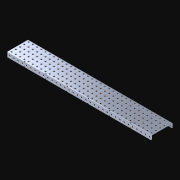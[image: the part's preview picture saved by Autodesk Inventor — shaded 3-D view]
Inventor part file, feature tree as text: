
AUTODESK INVENTOR PART (.ipt)
format: ipt  version: 2021 (Build 250183000, 183)  size: 2,489,344 bytes
history: native  units: in
note: dims shown in document units (in); Inventor stores cm internally (conversion verified against a paired STEP export)
features: extrude x239, other x239, sketch x4, pattern_linear x3
ambient origin geometry x8: Origin, YZ Plane, XZ Plane, XY Plane, X Axis, Y Axis, Z Axis, Center Point
bodies: Solid1 (feature_tree)
feature tree (485):
  pattern_linear  "Rectangular Pattern1"  Spacing1=0.182in  [1 undecoded]
  pattern_linear  "Rectangular Pattern2"  Spacing1=0.046in  [1 undecoded]
  pattern_linear  "Rectangular Pattern3"  Spacing1=0.5in  [1 undecoded]
  extrude  "Extrusion1"  Depth=0.046in
  sketch  "Sketch1"  dims[d0=0.182in]
  other  "Srf1"
  sketch  "Sketch2"  dims[d1=0.046in d2=0.0in]
  other  "Srf2"
  sketch  "Sketch3"  dims[d3=0.182in]
  other  "Srf3"
  other  "Srf4"
  other  "Srf5"
  other  "Srf6"
  other  "Srf7"
  other  "Srf8"
  other  "Srf9"
  other  "Srf10"
  other  "Srf11"
  other  "Srf12"
  other  "Srf13"
  other  "Srf14"
  other  "Srf15"
  other  "Srf16"
  other  "Srf17"
  other  "Srf18"
  other  "Srf19"
  other  "Srf20"
  other  "Srf21"
  other  "Srf22"
  other  "Srf23"
  other  "Srf24"
  other  "Srf25"
  other  "Srf26"
  other  "Srf27"
  other  "Srf28"
  other  "Srf29"
  other  "Srf30"
  other  "Srf31"
  other  "Srf32"
  other  "Srf33"
  other  "Srf34"
  other  "Srf35"
  other  "Srf36"
  other  "Srf38"
  other  "Srf39"
  other  "Srf40"
  other  "Srf41"
  other  "Srf42"
  other  "Srf43"
  other  "Srf44"
  other  "Srf45"
  other  "Srf46"
  other  "Srf47"
  other  "Srf48"
  other  "Srf49"
  other  "Srf50"
  other  "Srf51"
  other  "Srf52"
  other  "Srf53"
  other  "Srf54"
  other  "Srf55"
  other  "Srf56"
  other  "Srf57"
  other  "Srf58"
  other  "Srf59"
  other  "Srf60"
  other  "Srf61"
  other  "Srf62"
  other  "Srf63"
  other  "Srf64"
  other  "Srf65"
  other  "Srf66"
  other  "Srf67"
  other  "Srf68"
  other  "Srf69"
  other  "Srf70"
  other  "Srf72"
  other  "Srf73"
  other  "Srf74"
  other  "Srf75"
  other  "Srf76"
  other  "Srf77"
  other  "Srf78"
  other  "Srf79"
  other  "Srf80"
  other  "Srf81"
  other  "Srf82"
  other  "Srf83"
  other  "Srf84"
  other  "Srf85"
  other  "Srf86"
  other  "Srf87"
  other  "Srf88"
  other  "Srf89"
  other  "Srf90"
  other  "Srf91"
  other  "Srf92"
  other  "Srf93"
  other  "Srf94"
  other  "Srf95"
  other  "Srf96"
  other  "Srf97"
  other  "Srf98"
  other  "Srf99"
  other  "Srf100"
  other  "Srf101"
  other  "Srf102"
  other  "Srf103"
  other  "Srf104"
  other  "Srf105"
  other  "Srf107"
  other  "Srf108"
  other  "Srf109"
  other  "Srf110"
  other  "Srf111"
  other  "Srf112"
  other  "Srf113"
  other  "Srf114"
  other  "Srf115"
  other  "Srf116"
  other  "Srf117"
  other  "Srf118"
  other  "Srf119"
  other  "Srf120"
  other  "Srf121"
  other  "Srf122"
  other  "Srf123"
  other  "Srf124"
  other  "Srf125"
  other  "Srf126"
  other  "Srf127"
  other  "Srf128"
  other  "Srf129"
  other  "Srf130"
  other  "Srf131"
  other  "Srf132"
  other  "Srf133"
  other  "Srf134"
  other  "Srf135"
  other  "Srf136"
  other  "Srf137"
  other  "Srf138"
  other  "Srf139"
  other  "Srf140"
  other  "Srf142"
  other  "Srf143"
  other  "Srf144"
  other  "Srf145"
  other  "Srf146"
  other  "Srf147"
  other  "Srf148"
  other  "Srf149"
  other  "Srf150"
  other  "Srf151"
  other  "Srf152"
  other  "Srf153"
  other  "Srf154"
  other  "Srf155"
  other  "Srf156"
  other  "Srf157"
  other  "Srf158"
  other  "Srf159"
  other  "Srf160"
  other  "Srf161"
  other  "Srf162"
  other  "Srf163"
  other  "Srf164"
  other  "Srf165"
  other  "Srf166"
  other  "Srf167"
  other  "Srf168"
  other  "Srf169"
  other  "Srf170"
  other  "Srf171"
  other  "Srf172"
  other  "Srf173"
  other  "Srf174"
  other  "Srf175"
  other  "Srf177"
  other  "Srf178"
  other  "Srf179"
  other  "Srf180"
  other  "Srf181"
  other  "Srf182"
  other  "Srf183"
  other  "Srf184"
  other  "Srf185"
  other  "Srf186"
  other  "Srf187"
  other  "Srf188"
  other  "Srf189"
  other  "Srf190"
  other  "Srf191"
  other  "Srf192"
  other  "Srf193"
  other  "Srf194"
  other  "Srf195"
  other  "Srf196"
  other  "Srf197"
  other  "Srf198"
  other  "Srf199"
  other  "Srf200"
  other  "Srf201"
  other  "Srf202"
  other  "Srf203"
  other  "Srf204"
  other  "Srf205"
  other  "Srf206"
  other  "Srf207"
  other  "Srf208"
  other  "Srf209"
  other  "Srf210"
  other  "Srf212"
  other  "Srf213"
  other  "Srf214"
  other  "Srf215"
  other  "Srf216"
  other  "Srf217"
  other  "Srf218"
  other  "Srf219"
  other  "Srf220"
  other  "Srf221"
  other  "Srf222"
  other  "Srf223"
  other  "Srf224"
  other  "Srf225"
  other  "Srf226"
  other  "Srf227"
  other  "Srf228"
  other  "Srf229"
  other  "Srf230"
  other  "Srf231"
  other  "Srf232"
  other  "Srf233"
  other  "Srf234"
  other  "Srf235"
  other  "Srf236"
  other  "Srf237"
  other  "Srf238"
  other  "Srf239"
  other  "Srf240"
  other  "Srf241"
  other  "Srf242"
  other  "Srf243"
  other  "Srf244"
  sketch  "Sketch4"  dims[d4=0.046in d5=0.0in d6=0.182in d7=0.046in d8=0.0in d11=0.5in d12=13.3858in d14=0.5in d15=1.9685in d17=0.5in d18=13.3858in d20=0.5in d21=0.5in d22=0.0in]
  parser-record x1  (decoder bookkeeping rows leaked as tree rows — omitted from the tree; the rows remain in map.json)
  extrude  "ExtrusionSrf1"  Depth=0.046in
  extrude  "ExtrusionSrf2"  Depth=0.046in
  extrude  "ExtrusionSrf3"  Depth=0.046in
  extrude  "ExtrusionSrf4"  Depth=0.046in
  extrude  "ExtrusionSrf5"  Depth=0.046in
  extrude  "ExtrusionSrf6"  TaperAngle=0.0deg  [1 undecoded]
  extrude  "ExtrusionSrf7"  [1 undecoded]
  extrude  "ExtrusionSrf8"  [1 undecoded]
  extrude  "ExtrusionSrf9"  [1 undecoded]
  extrude  "ExtrusionSrf10"  [1 undecoded]
  extrude  "ExtrusionSrf11"  [1 undecoded]
  extrude  "ExtrusionSrf12"  [1 undecoded]
  extrude  "ExtrusionSrf13"  [1 undecoded]
  extrude  "ExtrusionSrf14"  [1 undecoded]
  extrude  "ExtrusionSrf15"  [1 undecoded]
  extrude  "ExtrusionSrf16"  [1 undecoded]
  extrude  "ExtrusionSrf17"  [1 undecoded]
  extrude  "ExtrusionSrf18"  [1 undecoded]
  extrude  "ExtrusionSrf19"  [1 undecoded]
  extrude  "ExtrusionSrf20"  [1 undecoded]
  extrude  "ExtrusionSrf21"  [1 undecoded]
  extrude  "ExtrusionSrf22"  [1 undecoded]
  extrude  "ExtrusionSrf23"  [1 undecoded]
  extrude  "ExtrusionSrf24"  [1 undecoded]
  extrude  "ExtrusionSrf25"  [1 undecoded]
  extrude  "ExtrusionSrf26"  [1 undecoded]
  extrude  "ExtrusionSrf27"  [1 undecoded]
  extrude  "ExtrusionSrf28"  [1 undecoded]
  extrude  "ExtrusionSrf29"  [1 undecoded]
  extrude  "ExtrusionSrf30"  [1 undecoded]
  extrude  "ExtrusionSrf31"  [1 undecoded]
  extrude  "ExtrusionSrf32"  [1 undecoded]
  extrude  "ExtrusionSrf33"  [1 undecoded]
  extrude  "ExtrusionSrf34"  [1 undecoded]
  extrude  "ExtrusionSrf35"  [1 undecoded]
  extrude  "ExtrusionSrf36"  [1 undecoded]
  extrude  "ExtrusionSrf38"  [1 undecoded]
  extrude  "ExtrusionSrf39"  [1 undecoded]
  extrude  "ExtrusionSrf40"  [1 undecoded]
  extrude  "ExtrusionSrf41"  [1 undecoded]
  extrude  "ExtrusionSrf42"  [1 undecoded]
  extrude  "ExtrusionSrf43"  [1 undecoded]
  extrude  "ExtrusionSrf44"  [1 undecoded]
  extrude  "ExtrusionSrf45"  [1 undecoded]
  extrude  "ExtrusionSrf46"  [1 undecoded]
  extrude  "ExtrusionSrf47"  [1 undecoded]
  extrude  "ExtrusionSrf48"  [1 undecoded]
  extrude  "ExtrusionSrf49"  [1 undecoded]
  extrude  "ExtrusionSrf50"  [1 undecoded]
  extrude  "ExtrusionSrf51"  [1 undecoded]
  extrude  "ExtrusionSrf52"  [1 undecoded]
  extrude  "ExtrusionSrf53"  [1 undecoded]
  extrude  "ExtrusionSrf54"  [1 undecoded]
  extrude  "ExtrusionSrf55"  [1 undecoded]
  extrude  "ExtrusionSrf56"  [1 undecoded]
  extrude  "ExtrusionSrf57"  [1 undecoded]
  extrude  "ExtrusionSrf58"  [1 undecoded]
  extrude  "ExtrusionSrf59"  [1 undecoded]
  extrude  "ExtrusionSrf60"  [1 undecoded]
  extrude  "ExtrusionSrf61"  [1 undecoded]
  extrude  "ExtrusionSrf62"  [1 undecoded]
  extrude  "ExtrusionSrf63"  [1 undecoded]
  extrude  "ExtrusionSrf64"  [1 undecoded]
  extrude  "ExtrusionSrf65"  [1 undecoded]
  extrude  "ExtrusionSrf66"  [1 undecoded]
  extrude  "ExtrusionSrf67"  [1 undecoded]
  extrude  "ExtrusionSrf68"  [1 undecoded]
  extrude  "ExtrusionSrf69"  [1 undecoded]
  extrude  "ExtrusionSrf70"  [1 undecoded]
  extrude  "ExtrusionSrf72"  [1 undecoded]
  extrude  "ExtrusionSrf73"  [1 undecoded]
  extrude  "ExtrusionSrf74"  [1 undecoded]
  extrude  "ExtrusionSrf75"  [1 undecoded]
  extrude  "ExtrusionSrf76"  [1 undecoded]
  extrude  "ExtrusionSrf77"  [1 undecoded]
  extrude  "ExtrusionSrf78"  [1 undecoded]
  extrude  "ExtrusionSrf79"  [1 undecoded]
  extrude  "ExtrusionSrf80"  [1 undecoded]
  extrude  "ExtrusionSrf81"  [1 undecoded]
  extrude  "ExtrusionSrf82"  [1 undecoded]
  extrude  "ExtrusionSrf83"  [1 undecoded]
  extrude  "ExtrusionSrf84"  [1 undecoded]
  extrude  "ExtrusionSrf85"  [1 undecoded]
  extrude  "ExtrusionSrf86"  [1 undecoded]
  extrude  "ExtrusionSrf87"  [1 undecoded]
  extrude  "ExtrusionSrf88"  [1 undecoded]
  extrude  "ExtrusionSrf89"  [1 undecoded]
  extrude  "ExtrusionSrf90"  [1 undecoded]
  extrude  "ExtrusionSrf91"  [1 undecoded]
  extrude  "ExtrusionSrf92"  [1 undecoded]
  extrude  "ExtrusionSrf93"  [1 undecoded]
  extrude  "ExtrusionSrf94"  [1 undecoded]
  extrude  "ExtrusionSrf95"  [1 undecoded]
  extrude  "ExtrusionSrf96"  [1 undecoded]
  extrude  "ExtrusionSrf97"  [1 undecoded]
  extrude  "ExtrusionSrf98"  [1 undecoded]
  extrude  "ExtrusionSrf99"  [1 undecoded]
  extrude  "ExtrusionSrf100"  [1 undecoded]
  extrude  "ExtrusionSrf101"  [1 undecoded]
  extrude  "ExtrusionSrf102"  [1 undecoded]
  extrude  "ExtrusionSrf103"  [1 undecoded]
  extrude  "ExtrusionSrf104"  [1 undecoded]
  extrude  "ExtrusionSrf105"  [1 undecoded]
  extrude  "ExtrusionSrf107"  [1 undecoded]
  extrude  "ExtrusionSrf108"  [1 undecoded]
  extrude  "ExtrusionSrf109"  [1 undecoded]
  extrude  "ExtrusionSrf110"  [1 undecoded]
  extrude  "ExtrusionSrf111"  [1 undecoded]
  extrude  "ExtrusionSrf112"  [1 undecoded]
  extrude  "ExtrusionSrf113"  [1 undecoded]
  extrude  "ExtrusionSrf114"  [1 undecoded]
  extrude  "ExtrusionSrf115"  [1 undecoded]
  extrude  "ExtrusionSrf116"  [1 undecoded]
  extrude  "ExtrusionSrf117"  [1 undecoded]
  extrude  "ExtrusionSrf118"  [1 undecoded]
  extrude  "ExtrusionSrf119"  [1 undecoded]
  extrude  "ExtrusionSrf120"  [1 undecoded]
  extrude  "ExtrusionSrf121"  [1 undecoded]
  extrude  "ExtrusionSrf122"  [1 undecoded]
  extrude  "ExtrusionSrf123"  [1 undecoded]
  extrude  "ExtrusionSrf124"  [1 undecoded]
  extrude  "ExtrusionSrf125"  [1 undecoded]
  extrude  "ExtrusionSrf126"  [1 undecoded]
  extrude  "ExtrusionSrf127"  [1 undecoded]
  extrude  "ExtrusionSrf128"  [1 undecoded]
  extrude  "ExtrusionSrf129"  [1 undecoded]
  extrude  "ExtrusionSrf130"  [1 undecoded]
  extrude  "ExtrusionSrf131"  [1 undecoded]
  extrude  "ExtrusionSrf132"  [1 undecoded]
  extrude  "ExtrusionSrf133"  [1 undecoded]
  extrude  "ExtrusionSrf134"  [1 undecoded]
  extrude  "ExtrusionSrf135"  [1 undecoded]
  extrude  "ExtrusionSrf136"  [1 undecoded]
  extrude  "ExtrusionSrf137"  [1 undecoded]
  extrude  "ExtrusionSrf138"  [1 undecoded]
  extrude  "ExtrusionSrf139"  [1 undecoded]
  extrude  "ExtrusionSrf140"  [1 undecoded]
  extrude  "ExtrusionSrf142"  [1 undecoded]
  extrude  "ExtrusionSrf143"  [1 undecoded]
  extrude  "ExtrusionSrf144"  [1 undecoded]
  extrude  "ExtrusionSrf145"  [1 undecoded]
  extrude  "ExtrusionSrf146"  [1 undecoded]
  extrude  "ExtrusionSrf147"  [1 undecoded]
  extrude  "ExtrusionSrf148"  [1 undecoded]
  extrude  "ExtrusionSrf149"  [1 undecoded]
  extrude  "ExtrusionSrf150"  [1 undecoded]
  extrude  "ExtrusionSrf151"  [1 undecoded]
  extrude  "ExtrusionSrf152"  [1 undecoded]
  extrude  "ExtrusionSrf153"  [1 undecoded]
  extrude  "ExtrusionSrf154"  [1 undecoded]
  extrude  "ExtrusionSrf155"  [1 undecoded]
  extrude  "ExtrusionSrf156"  [1 undecoded]
  extrude  "ExtrusionSrf157"  [1 undecoded]
  extrude  "ExtrusionSrf158"  [1 undecoded]
  extrude  "ExtrusionSrf159"  [1 undecoded]
  extrude  "ExtrusionSrf160"  [1 undecoded]
  extrude  "ExtrusionSrf161"  [1 undecoded]
  extrude  "ExtrusionSrf162"  [1 undecoded]
  extrude  "ExtrusionSrf163"  [1 undecoded]
  extrude  "ExtrusionSrf164"  [1 undecoded]
  extrude  "ExtrusionSrf165"  [1 undecoded]
  extrude  "ExtrusionSrf166"  [1 undecoded]
  extrude  "ExtrusionSrf167"  [1 undecoded]
  extrude  "ExtrusionSrf168"  [1 undecoded]
  extrude  "ExtrusionSrf169"  [1 undecoded]
  extrude  "ExtrusionSrf170"  [1 undecoded]
  extrude  "ExtrusionSrf171"  [1 undecoded]
  extrude  "ExtrusionSrf172"  [1 undecoded]
  extrude  "ExtrusionSrf173"  [1 undecoded]
  extrude  "ExtrusionSrf174"  [1 undecoded]
  extrude  "ExtrusionSrf175"  [1 undecoded]
  extrude  "ExtrusionSrf177"  [1 undecoded]
  extrude  "ExtrusionSrf178"  [1 undecoded]
  extrude  "ExtrusionSrf179"  [1 undecoded]
  extrude  "ExtrusionSrf180"  [1 undecoded]
  extrude  "ExtrusionSrf181"  [1 undecoded]
  extrude  "ExtrusionSrf182"  [1 undecoded]
  extrude  "ExtrusionSrf183"  [1 undecoded]
  extrude  "ExtrusionSrf184"  [1 undecoded]
  extrude  "ExtrusionSrf185"  [1 undecoded]
  extrude  "ExtrusionSrf186"  [1 undecoded]
  extrude  "ExtrusionSrf187"  [1 undecoded]
  extrude  "ExtrusionSrf188"  [1 undecoded]
  extrude  "ExtrusionSrf189"  [1 undecoded]
  extrude  "ExtrusionSrf190"  [1 undecoded]
  extrude  "ExtrusionSrf191"  [1 undecoded]
  extrude  "ExtrusionSrf192"  [1 undecoded]
  extrude  "ExtrusionSrf193"  [1 undecoded]
  extrude  "ExtrusionSrf194"  [1 undecoded]
  extrude  "ExtrusionSrf195"  [1 undecoded]
  extrude  "ExtrusionSrf196"  [1 undecoded]
  extrude  "ExtrusionSrf197"  [1 undecoded]
  extrude  "ExtrusionSrf198"  [1 undecoded]
  extrude  "ExtrusionSrf199"  [1 undecoded]
  extrude  "ExtrusionSrf200"  [1 undecoded]
  extrude  "ExtrusionSrf201"  [1 undecoded]
  extrude  "ExtrusionSrf202"  [1 undecoded]
  extrude  "ExtrusionSrf203"  [1 undecoded]
  extrude  "ExtrusionSrf204"  [1 undecoded]
  extrude  "ExtrusionSrf205"  [1 undecoded]
  extrude  "ExtrusionSrf206"  [1 undecoded]
  extrude  "ExtrusionSrf207"  [1 undecoded]
  extrude  "ExtrusionSrf208"  [1 undecoded]
  extrude  "ExtrusionSrf209"  [1 undecoded]
  extrude  "ExtrusionSrf210"  [1 undecoded]
  extrude  "ExtrusionSrf212"  [1 undecoded]
  extrude  "ExtrusionSrf213"  [1 undecoded]
  extrude  "ExtrusionSrf214"  [1 undecoded]
  extrude  "ExtrusionSrf215"  [1 undecoded]
  extrude  "ExtrusionSrf216"  [1 undecoded]
  extrude  "ExtrusionSrf217"  [1 undecoded]
  extrude  "ExtrusionSrf218"  [1 undecoded]
  extrude  "ExtrusionSrf219"  [1 undecoded]
  extrude  "ExtrusionSrf220"  [1 undecoded]
  extrude  "ExtrusionSrf221"  [1 undecoded]
  extrude  "ExtrusionSrf222"  [1 undecoded]
  extrude  "ExtrusionSrf223"  [1 undecoded]
  extrude  "ExtrusionSrf224"  [1 undecoded]
  extrude  "ExtrusionSrf225"  [1 undecoded]
  extrude  "ExtrusionSrf226"  [1 undecoded]
  extrude  "ExtrusionSrf227"  [1 undecoded]
  extrude  "ExtrusionSrf228"  [1 undecoded]
  extrude  "ExtrusionSrf229"  [1 undecoded]
  extrude  "ExtrusionSrf230"  [1 undecoded]
  extrude  "ExtrusionSrf231"  [1 undecoded]
  extrude  "ExtrusionSrf232"  [1 undecoded]
  extrude  "ExtrusionSrf233"  [1 undecoded]
  extrude  "ExtrusionSrf234"  [1 undecoded]
  extrude  "ExtrusionSrf235"  [1 undecoded]
  extrude  "ExtrusionSrf236"  [1 undecoded]
  extrude  "ExtrusionSrf237"  [1 undecoded]
  extrude  "ExtrusionSrf238"  [1 undecoded]
  extrude  "ExtrusionSrf239"  [1 undecoded]
  extrude  "ExtrusionSrf240"  [1 undecoded]
  extrude  "ExtrusionSrf241"  [1 undecoded]
  extrude  "ExtrusionSrf242"  [1 undecoded]
  extrude  "ExtrusionSrf243"  [1 undecoded]
  extrude  "ExtrusionSrf244"  [1 undecoded]
note: 236 required parameter values undecoded (feature->parameter linkage not recoverable at this tier; creation-order binding heuristic only, values carry confidence <= 0.55)
